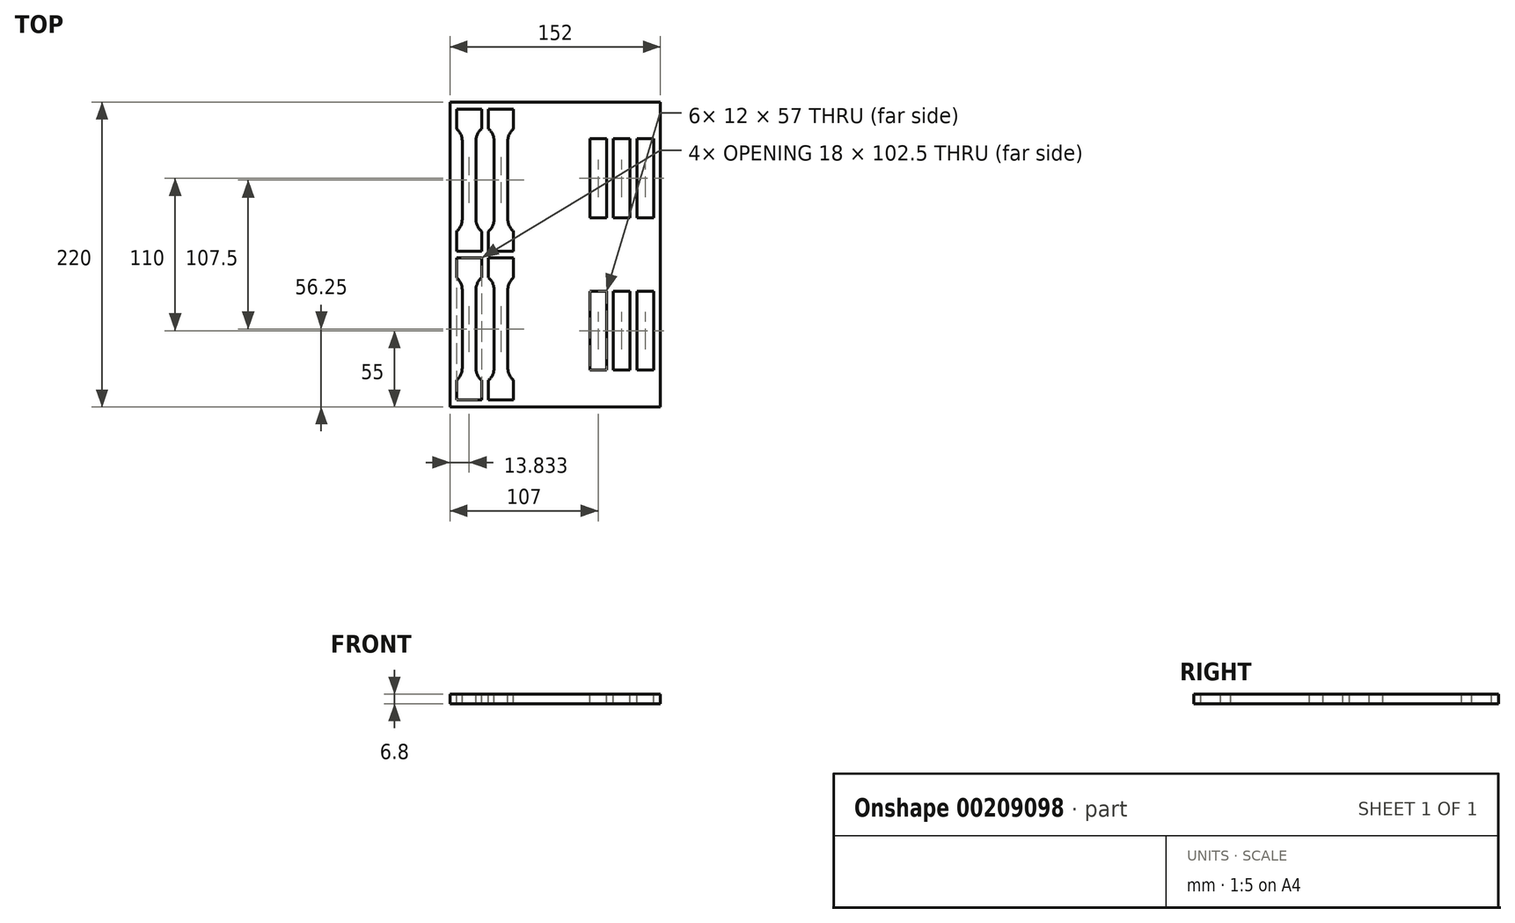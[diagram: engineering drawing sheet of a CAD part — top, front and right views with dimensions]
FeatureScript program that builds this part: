
annotation { "Feature Type Name" : "Feature", "Feature Type Description" : "" }
export const myFeature = defineFeature(function(context is Context, id is Id, definition is map)
    precondition{}
    {
        {
            var Q0;
            Q0=qCreatedBy(makeId("Front.planeOp"),FACE);
            var sketch = newSketch(context, id + "F0", { "sketchPlane" : qUnion([Q0])});
            skLineSegment(sketch, "E0.left", {"start": v(3.05, -60.3) * mm, "end": v(3.05, 60.3) * mm});
            skLineSegment(sketch, "E0.right", {"start": v(-3.05, -60.3) * mm, "end": v(-3.05, 60.3) * mm});
            skPoint(sketch, "E0.middle", {"position": v(0, 0) * mm});
            skLineSegment(sketch, "E1.top", {"start": v(76, 76) * mm, "end": v(-76, 76) * mm});
            skLineSegment(sketch, "E1.left", {"start": v(76, 69.2) * mm, "end": v(76, 76) * mm});
            skLineSegment(sketch, "E1.right", {"start": v(-76, 69.2) * mm, "end": v(-76, 76) * mm});
            skPoint(sketch, "E1.middle", {"position": v(0, 72.6) * mm});
            skPoint(sketch, "E1.middle.positionSnap0", {"position": v(0, 69.2) * mm});
            skPoint(sketch, "E1.centerSnap0", {"position": v(0, 69.2) * mm});
            skLineSegment(sketch, "E2.top", {"start": v(76, -76) * mm, "end": v(-76, -76) * mm});
            skLineSegment(sketch, "E2.left", {"start": v(76, -69.2) * mm, "end": v(76, -76) * mm});
            skLineSegment(sketch, "E2.right", {"start": v(-76, -69.2) * mm, "end": v(-76, -76) * mm});
            skPoint(sketch, "E2.middle", {"position": v(0, -72.6) * mm});
            skLineSegment(sketch, "E3", {"start": v(-76, 69.2) * mm, "end": v(-11.95, 69.2) * mm});
            skLineSegment(sketch, "E4", {"start": v(11.95, 69.2) * mm, "end": v(76, 69.2) * mm});
            skLineSegment(sketch, "E5", {"start": v(11.95, -69.2) * mm, "end": v(76, -69.2) * mm});
            skLineSegment(sketch, "E6", {"start": v(-11.95, -69.2) * mm, "end": v(-76, -69.2) * mm});
            skPoint(sketch, "E7.visualSharp", {"position": v(-3.05, 69.2) * mm});
            skArc(sketch, "E7.filletArc", {"start": v(-3.05, 60.3) * mm, "mid": v(-5.66, 66.6) * mm, "end": v(-11.95, 69.2) * mm});
            skPoint(sketch, "E8.visualSharp", {"position": v(3.05, 69.2) * mm});
            skArc(sketch, "E8.filletArc", {"start": v(11.95, 69.2) * mm, "mid": v(5.66, 66.6) * mm, "end": v(3.05, 60.3) * mm});
            skPoint(sketch, "E9.visualSharp", {"position": v(-3.05, -69.2) * mm});
            skArc(sketch, "E9.filletArc", {"start": v(-11.95, -69.2) * mm, "mid": v(-5.66, -66.6) * mm, "end": v(-3.05, -60.3) * mm});
            skPoint(sketch, "E10.visualSharp", {"position": v(3.05, -69.2) * mm});
            skArc(sketch, "E10.filletArc", {"start": v(3.05, -60.3) * mm, "mid": v(5.66, -66.6) * mm, "end": v(11.95, -69.2) * mm});
            skPoint(sketch, "E11.startSnap0", {"position": v(-5.66, 66.6) * mm});
            skPoint(sketch, "E11.endSnap0", {"position": v(-5.66, 66.6) * mm});
            skPoint(sketch, "E12.startSnap0", {"position": v(-5.66, -66.6) * mm});
            skSolve(sketch);
        }
        {
            var Q0;
            Q0=makeQuery(id+"F0.imprint","IMPRINT",FACE,{"disambiguationData":[TD([[makeQuery(id+"F0.imprint","IMPRINT",EDGE,{"derivedFrom":sQuery(id+"F0.wireOp",EDGE,"E0.left")}),1.0]])]});
            extrude(context, id + "F1", {"entities" : qUnion([Q0]), "depth" : 220 * mm, "symmetric" : true});
        }
        {
            var Q0;
            Q0=makeQuery(id+"F1.opExtrude","SWEPT_FACE",FACE,{"disambiguationData":[OSD([sQuery(id+"F0.wireOp",EDGE,"E1.top")])]});
            var sketch = newSketch(context, id + "F2", { "sketchPlane" : qUnion([Q0])});
            skLineSegment(sketch, "E13.bottom", {"start": v(0, -4) * mm, "end": v(-76, -4) * mm});
            skLineSegment(sketch, "E13.top", {"start": v(0, 4) * mm, "end": v(-76, 4) * mm});
            skLineSegment(sketch, "E13.left", {"start": v(0, -4) * mm, "end": v(0, 4) * mm});
            skLineSegment(sketch, "E13.right", {"start": v(-76, -4) * mm, "end": v(-76, 4) * mm});
            skPoint(sketch, "E13.middle", {"position": v(-38, 0) * mm});
            skSolve(sketch);
        }
        {
            var Q0;
            Q0=makeQuery(id+"F2.imprint","IMPRINT",FACE,{"disambiguationData":[TD([[makeQuery(id+"F2.imprint","IMPRINT",EDGE,{"derivedFrom":sQuery(id+"F2.wireOp",EDGE,"E13.bottom")}),-1.0]])]});
            extrude(context, id + "F3", {"entities" : qUnion([Q0]), "operationType" : NewBodyOperationType.ADD, "oppositeDirection" : true, "depth" : 152 * mm});
        }
        {
            var Q0;
            Q0=makeQuery(id+"F1.opExtrude","SWEPT_FACE",FACE,{"disambiguationData":[OSD([sQuery(id+"F0.wireOp",EDGE,"E1.top")])]});
            var sketch = newSketch(context, id + "F4", { "sketchPlane" : qUnion([Q0])});
            skLineSegment(sketch, "E14.bottom", {"start": v(54, -83.5) * mm, "end": v(42, -83.5) * mm});
            skLineSegment(sketch, "E14.top", {"start": v(54, -26.5) * mm, "end": v(42, -26.5) * mm});
            skLineSegment(sketch, "E14.left", {"start": v(54, -83.5) * mm, "end": v(54, -26.5) * mm});
            skLineSegment(sketch, "E14.right", {"start": v(42, -83.5) * mm, "end": v(42, -26.5) * mm});
            skLineSegment(sketch, "E15.bottom", {"start": v(71, -26.5) * mm, "end": v(59, -26.5) * mm});
            skLineSegment(sketch, "E15.top", {"start": v(71, -83.5) * mm, "end": v(59, -83.5) * mm});
            skLineSegment(sketch, "E15.left", {"start": v(71, -26.5) * mm, "end": v(71, -83.5) * mm});
            skLineSegment(sketch, "E15.right", {"start": v(59, -26.5) * mm, "end": v(59, -83.5) * mm});
            skLineSegment(sketch, "E16.MirrorCS", {"start": v(25, -26.5) * mm, "end": v(25, -83.5) * mm});
            skLineSegment(sketch, "E17.MirrorCS", {"start": v(37, -26.5) * mm, "end": v(37, -83.5) * mm});
            skLineSegment(sketch, "E18.MirrorCS", {"start": v(25, -26.5) * mm, "end": v(37, -26.5) * mm});
            skLineSegment(sketch, "E19.MirrorCS", {"start": v(25, -83.5) * mm, "end": v(37, -83.5) * mm});
            skLineSegment(sketch, "E20.MirrorCS", {"start": v(71, 26.5) * mm, "end": v(71, 83.5) * mm});
            skLineSegment(sketch, "E21.MirrorCS", {"start": v(71, 83.5) * mm, "end": v(59, 83.5) * mm});
            skLineSegment(sketch, "E22.MirrorCS", {"start": v(54, 26.5) * mm, "end": v(42, 26.5) * mm});
            skLineSegment(sketch, "E23.MirrorCS", {"start": v(59, 26.5) * mm, "end": v(59, 83.5) * mm});
            skLineSegment(sketch, "E24.MirrorCS", {"start": v(25, 83.5) * mm, "end": v(37, 83.5) * mm});
            skLineSegment(sketch, "E25.MirrorCS", {"start": v(71, 26.5) * mm, "end": v(59, 26.5) * mm});
            skLineSegment(sketch, "E26.MirrorCS", {"start": v(25, 26.5) * mm, "end": v(25, 83.5) * mm});
            skLineSegment(sketch, "E27.MirrorCS", {"start": v(54, 83.5) * mm, "end": v(42, 83.5) * mm});
            skLineSegment(sketch, "E28.MirrorCS", {"start": v(37, 26.5) * mm, "end": v(37, 83.5) * mm});
            skLineSegment(sketch, "E29.MirrorCS", {"start": v(25, 26.5) * mm, "end": v(37, 26.5) * mm});
            skLineSegment(sketch, "E30.MirrorCS", {"start": v(42, 83.5) * mm, "end": v(42, 26.5) * mm});
            skLineSegment(sketch, "E31.MirrorCS", {"start": v(54, 83.5) * mm, "end": v(54, 26.5) * mm});
            skLineSegment(sketch, "E32.bottom", {"start": v(-53.17, 2.5) * mm, "end": v(-71.17, 2.5) * mm});
            skLineSegment(sketch, "E32.top", {"start": v(-53.17, 105) * mm, "end": v(-71.17, 105) * mm});
            skLineSegment(sketch, "E33.left", {"start": v(-57.17, 25.25) * mm, "end": v(-57.17, 82.25) * mm});
            skLineSegment(sketch, "E33.right", {"start": v(-67.17, 25.25) * mm, "end": v(-67.17, 82.25) * mm});
            skArc(sketch, "E34", {"start": v(-57.17, 82.25) * mm, "mid": v(-56.12, 86.94) * mm, "end": v(-53.17, 90.74) * mm});
            skArc(sketch, "E35", {"start": v(-67.17, 82.25) * mm, "mid": v(-68.22, 86.94) * mm, "end": v(-71.17, 90.74) * mm});
            skArc(sketch, "E36", {"start": v(-67.17, 25.25) * mm, "mid": v(-68.22, 20.56) * mm, "end": v(-71.17, 16.76) * mm});
            skArc(sketch, "E37", {"start": v(-57.17, 25.25) * mm, "mid": v(-56.12, 20.56) * mm, "end": v(-53.17, 16.76) * mm});
            skLineSegment(sketch, "E38", {"start": v(-71.17, 105) * mm, "end": v(-71.17, 90.74) * mm});
            skLineSegment(sketch, "E39", {"start": v(-53.17, 105) * mm, "end": v(-53.17, 90.74) * mm});
            skLineSegment(sketch, "E40", {"start": v(-71.17, 16.76) * mm, "end": v(-71.17, 2.5) * mm});
            skLineSegment(sketch, "E41", {"start": v(-53.17, 16.76) * mm, "end": v(-53.17, 2.5) * mm});
            skArc(sketch, "E42.MirrorCS", {"start": v(-44.17, 82.25) * mm, "mid": v(-45.22, 86.94) * mm, "end": v(-48.17, 90.74) * mm});
            skArc(sketch, "E43.MirrorCS", {"start": v(-44.17, 25.25) * mm, "mid": v(-45.22, 20.56) * mm, "end": v(-48.17, 16.76) * mm});
            skLineSegment(sketch, "E44.MirrorCS", {"start": v(-34.17, 25.25) * mm, "end": v(-34.17, 82.25) * mm});
            skArc(sketch, "E45.MirrorCS", {"start": v(-34.17, 82.25) * mm, "mid": v(-33.12, 86.94) * mm, "end": v(-30.17, 90.74) * mm});
            skLineSegment(sketch, "E46.MirrorCS", {"start": v(-48.17, 105) * mm, "end": v(-30.17, 105) * mm});
            skLineSegment(sketch, "E47.MirrorCS", {"start": v(-30.17, 16.76) * mm, "end": v(-30.17, 2.5) * mm});
            skLineSegment(sketch, "E48.MirrorCS", {"start": v(-48.17, 16.76) * mm, "end": v(-48.17, 2.5) * mm});
            skArc(sketch, "E49.MirrorCS", {"start": v(-34.17, 25.25) * mm, "mid": v(-33.12, 20.56) * mm, "end": v(-30.17, 16.76) * mm});
            skLineSegment(sketch, "E50.MirrorCS", {"start": v(-48.17, 2.5) * mm, "end": v(-30.17, 2.5) * mm});
            skLineSegment(sketch, "E51.MirrorCS", {"start": v(-30.17, 105) * mm, "end": v(-30.17, 90.74) * mm});
            skLineSegment(sketch, "E52.MirrorCS", {"start": v(-44.17, 25.25) * mm, "end": v(-44.17, 82.25) * mm});
            skLineSegment(sketch, "E53.MirrorCS", {"start": v(-48.17, 105) * mm, "end": v(-48.17, 90.74) * mm});
            skLineSegment(sketch, "E54.MirrorCS", {"start": v(-53.17, -105) * mm, "end": v(-53.17, -90.74) * mm});
            skLineSegment(sketch, "E55.MirrorCS", {"start": v(-53.17, -2.5) * mm, "end": v(-71.17, -2.5) * mm});
            skLineSegment(sketch, "E56.MirrorCS", {"start": v(-67.17, -25.25) * mm, "end": v(-67.17, -82.25) * mm});
            skArc(sketch, "E57.MirrorCS", {"start": v(-67.17, -82.25) * mm, "mid": v(-68.22, -86.94) * mm, "end": v(-71.17, -90.74) * mm});
            skLineSegment(sketch, "E58.MirrorCS", {"start": v(-71.17, -16.76) * mm, "end": v(-71.17, -2.5) * mm});
            skArc(sketch, "E59.MirrorCS", {"start": v(-57.17, -25.25) * mm, "mid": v(-56.12, -20.56) * mm, "end": v(-53.17, -16.76) * mm});
            skArc(sketch, "E60.MirrorCS", {"start": v(-44.17, -25.25) * mm, "mid": v(-45.22, -20.56) * mm, "end": v(-48.17, -16.76) * mm});
            skLineSegment(sketch, "E61.MirrorCS", {"start": v(-30.17, -105) * mm, "end": v(-30.17, -90.74) * mm});
            skLineSegment(sketch, "E62.MirrorCS", {"start": v(-48.17, -2.5) * mm, "end": v(-30.17, -2.5) * mm});
            skArc(sketch, "E63.MirrorCS", {"start": v(-44.17, -82.25) * mm, "mid": v(-45.22, -86.94) * mm, "end": v(-48.17, -90.74) * mm});
            skLineSegment(sketch, "E64.MirrorCS", {"start": v(-48.17, -16.76) * mm, "end": v(-48.17, -2.5) * mm});
            skArc(sketch, "E65.MirrorCS", {"start": v(-34.17, -25.25) * mm, "mid": v(-33.12, -20.56) * mm, "end": v(-30.17, -16.76) * mm});
            skLineSegment(sketch, "E66.MirrorCS", {"start": v(-48.17, -105) * mm, "end": v(-30.17, -105) * mm});
            skLineSegment(sketch, "E67.MirrorCS", {"start": v(-34.17, -25.25) * mm, "end": v(-34.17, -82.25) * mm});
            skLineSegment(sketch, "E68.MirrorCS", {"start": v(-57.17, -25.25) * mm, "end": v(-57.17, -82.25) * mm});
            skLineSegment(sketch, "E69.MirrorCS", {"start": v(-71.17, -105) * mm, "end": v(-71.17, -90.74) * mm});
            skLineSegment(sketch, "E70.MirrorCS", {"start": v(-53.17, -105) * mm, "end": v(-71.17, -105) * mm});
            skArc(sketch, "E71.MirrorCS", {"start": v(-34.17, -82.25) * mm, "mid": v(-33.12, -86.94) * mm, "end": v(-30.17, -90.74) * mm});
            skLineSegment(sketch, "E72.MirrorCS", {"start": v(-53.17, -16.76) * mm, "end": v(-53.17, -2.5) * mm});
            skLineSegment(sketch, "E73.MirrorCS", {"start": v(-48.17, -105) * mm, "end": v(-48.17, -90.74) * mm});
            skLineSegment(sketch, "E74.MirrorCS", {"start": v(-30.17, -16.76) * mm, "end": v(-30.17, -2.5) * mm});
            skLineSegment(sketch, "E75.MirrorCS", {"start": v(-44.17, -25.25) * mm, "end": v(-44.17, -82.25) * mm});
            skArc(sketch, "E76.MirrorCS", {"start": v(-57.17, -82.25) * mm, "mid": v(-56.12, -86.94) * mm, "end": v(-53.17, -90.74) * mm});
            skArc(sketch, "E77.MirrorCS", {"start": v(-67.17, -25.25) * mm, "mid": v(-68.22, -20.56) * mm, "end": v(-71.17, -16.76) * mm});
            skSolve(sketch);
        }
        {
            var Q0;
            Q0=makeQuery(id+"F4.imprint","IMPRINT",FACE,{"disambiguationData":[TD([[makeQuery(id+"F4.imprint","IMPRINT",EDGE,{"derivedFrom":sQuery(id+"F4.wireOp",EDGE,"c36ddfbc-2ab3-428e-8b08-6e1e0dfc5d031.MirrorCS")}),1.0]])]});
            var Q1;
            Q1=makeQuery(id+"F4.imprint","IMPRINT",FACE,{"disambiguationData":[TD([[makeQuery(id+"F4.imprint","IMPRINT",EDGE,{"derivedFrom":sQuery(id+"F4.wireOp",EDGE,"c36ddfbc-2ab3-428e-8b08-6e1e0dfc5d0312.MirrorCS")}),-1.0]])]});
            var Q2;
            Q2=makeQuery(id+"F4.imprint","IMPRINT",FACE,{"disambiguationData":[TD([[makeQuery(id+"F4.imprint","IMPRINT",EDGE,{"derivedFrom":sQuery(id+"F4.wireOp",EDGE,"onuLAD5o-24AH-9kwD-0ncM-cT8nqrzVXT6I.bottom")}),1.0]])]});
            var Q3;
            {var subQ0=sQuery(id+"F4.wireOp",EDGE,"269746e7-c3dc-48b9-b7d4-6ec56124e9381.MirrorCS");Q3=makeQuery(id+"F4.imprint","IMPRINT",FACE,{"disambiguationData":[TD([[makeQuery(id+"F4.imprint","IMPRINT",EDGE,{"derivedFrom":subQ0}),1.0]])]});}
            var Q4;
            Q4=makeQuery(id+"F4.imprint","IMPRINT",FACE,{"disambiguationData":[TD([[makeQuery(id+"F4.imprint","IMPRINT",EDGE,{"derivedFrom":sQuery(id+"F4.wireOp",EDGE,"2LnyczaG-wFis-RWd3-eKWl-CX4d7uCzCTR5.bottom")}),1.0]])]});
            var Q5;
            Q5=makeQuery(id+"F4.imprint","IMPRINT",FACE,{"disambiguationData":[TD([[makeQuery(id+"F4.imprint","IMPRINT",EDGE,{"derivedFrom":sQuery(id+"F4.wireOp",EDGE,"f61618ef-a7ac-4b52-be35-deefb2d7ca773.MirrorCS")}),-1.0]])]});
            var Q6;
            {var subQ1=sQuery(id+"F4.wireOp",EDGE,"0a2dd84e-1d9f-4d7e-a446-57e104b887331.MirrorCS");Q6=makeQuery(id+"F4.imprint","IMPRINT",FACE,{"disambiguationData":[TD([[makeQuery(id+"F4.imprint","IMPRINT",EDGE,{"derivedFrom":subQ1}),-1.0]])]});}
            var Q7;
            Q7=makeQuery(id+"F4.imprint","IMPRINT",FACE,{"disambiguationData":[TD([[makeQuery(id+"F4.imprint","IMPRINT",EDGE,{"derivedFrom":sQuery(id+"F4.wireOp",EDGE,"0a2dd84e-1d9f-4d7e-a446-57e104b887337.MirrorCS")}),1.0]])]});
            var Q8;
            Q8=makeQuery(id+"F4.imprint","IMPRINT",FACE,{"disambiguationData":[TD([[makeQuery(id+"F4.imprint","IMPRINT",EDGE,{"derivedFrom":sQuery(id+"F4.wireOp",EDGE,"0a2dd84e-1d9f-4d7e-a446-57e104b887332.MirrorCS")}),1.0]])]});
            var Q9;
            Q9=makeQuery(id+"F4.imprint","IMPRINT",FACE,{"disambiguationData":[TD([[makeQuery(id+"F4.imprint","IMPRINT",EDGE,{"derivedFrom":sQuery(id+"F4.wireOp",EDGE,"E42.MirrorCS")}),-1.0]])]});
            var Q10;
            Q10=makeQuery(id+"F4.imprint","IMPRINT",FACE,{"disambiguationData":[TD([[makeQuery(id+"F4.imprint","IMPRINT",EDGE,{"derivedFrom":sQuery(id+"F4.wireOp",EDGE,"E32.bottom")}),-1.0]])]});
            var Q11;
            Q11=makeQuery(id+"F4.imprint","IMPRINT",FACE,{"disambiguationData":[TD([[makeQuery(id+"F4.imprint","IMPRINT",EDGE,{"derivedFrom":sQuery(id+"F4.wireOp",EDGE,"E24.MirrorCS")}),-1.0]])]});
            var Q12;
            Q12=makeQuery(id+"F4.imprint","IMPRINT",FACE,{"disambiguationData":[TD([[makeQuery(id+"F4.imprint","IMPRINT",EDGE,{"derivedFrom":sQuery(id+"F4.wireOp",EDGE,"E22.MirrorCS")}),-1.0]])]});
            var Q13;
            Q13=makeQuery(id+"F4.imprint","IMPRINT",FACE,{"disambiguationData":[TD([[makeQuery(id+"F4.imprint","IMPRINT",EDGE,{"derivedFrom":sQuery(id+"F4.wireOp",EDGE,"E20.MirrorCS")}),1.0]])]});
            var Q14;
            Q14=makeQuery(id+"F4.imprint","IMPRINT",FACE,{"disambiguationData":[TD([[makeQuery(id+"F4.imprint","IMPRINT",EDGE,{"derivedFrom":sQuery(id+"F4.wireOp",EDGE,"E16.MirrorCS")}),1.0]])]});
            var Q15;
            Q15=makeQuery(id+"F4.imprint","IMPRINT",FACE,{"disambiguationData":[TD([[makeQuery(id+"F4.imprint","IMPRINT",EDGE,{"derivedFrom":sQuery(id+"F4.wireOp",EDGE,"E14.bottom")}),-1.0]])]});
            var Q16;
            Q16=makeQuery(id+"F4.imprint","IMPRINT",FACE,{"disambiguationData":[TD([[makeQuery(id+"F4.imprint","IMPRINT",EDGE,{"derivedFrom":sQuery(id+"F4.wireOp",EDGE,"E15.bottom")}),1.0]])]});
            var Q17;
            Q17=makeQuery(id+"F4.imprint","IMPRINT",FACE,{"disambiguationData":[TD([[makeQuery(id+"F4.imprint","IMPRINT",EDGE,{"derivedFrom":sQuery(id+"F4.wireOp",EDGE,"E54.MirrorCS")}),1.0]])]});
            var Q18;
            Q18=makeQuery(id+"F4.imprint","IMPRINT",FACE,{"disambiguationData":[TD([[makeQuery(id+"F4.imprint","IMPRINT",EDGE,{"derivedFrom":sQuery(id+"F4.wireOp",EDGE,"E60.MirrorCS")}),-1.0]])]});
            extrude(context, id + "F5", {"entities" : qUnion([Q0, Q1, Q2, Q3, Q4, Q5, Q6, Q7, Q8, Q9, Q10, Q11, Q12, Q13, Q14, Q15, Q16, Q17, Q18]), "operationType" : NewBodyOperationType.REMOVE, "oppositeDirection" : true, "depth" : 152 * mm});
        }
        {
            var Q0;
            Q0=makeQuery(id+"F1.opExtrude","SWEPT_FACE",FACE,{"disambiguationData":[OSD([sQuery(id+"F0.wireOp",EDGE,"E2.top")])]});
            var sketch = newSketch(context, id + "F6", { "sketchPlane" : qUnion([Q0])});
            skLineSegment(sketch, "E78.bottom", {"start": v(76, -110) * mm, "end": v(-76, -110) * mm});
            skLineSegment(sketch, "E78.top", {"start": v(76, 110) * mm, "end": v(-76, 110) * mm});
            skLineSegment(sketch, "E78.left", {"start": v(76, -110) * mm, "end": v(76, 110) * mm});
            skLineSegment(sketch, "E78.right", {"start": v(-76, -110) * mm, "end": v(-76, 110) * mm});
            skPoint(sketch, "E78.middle", {"position": v(0, 0) * mm});
            skSolve(sketch);
        }
        {
            var Q0;
            Q0=makeQuery(id+"F6.imprint","IMPRINT",FACE,{"disambiguationData":[TD([[makeQuery(id+"F6.imprint","IMPRINT",EDGE,{"derivedFrom":sQuery(id+"F6.wireOp",EDGE,"E78.bottom")}),-1.0]])]});
            extrude(context, id + "F7", {"entities" : qUnion([Q0]), "operationType" : NewBodyOperationType.REMOVE, "oppositeDirection" : true, "depth" : 145.2 * mm});
        }
    });
